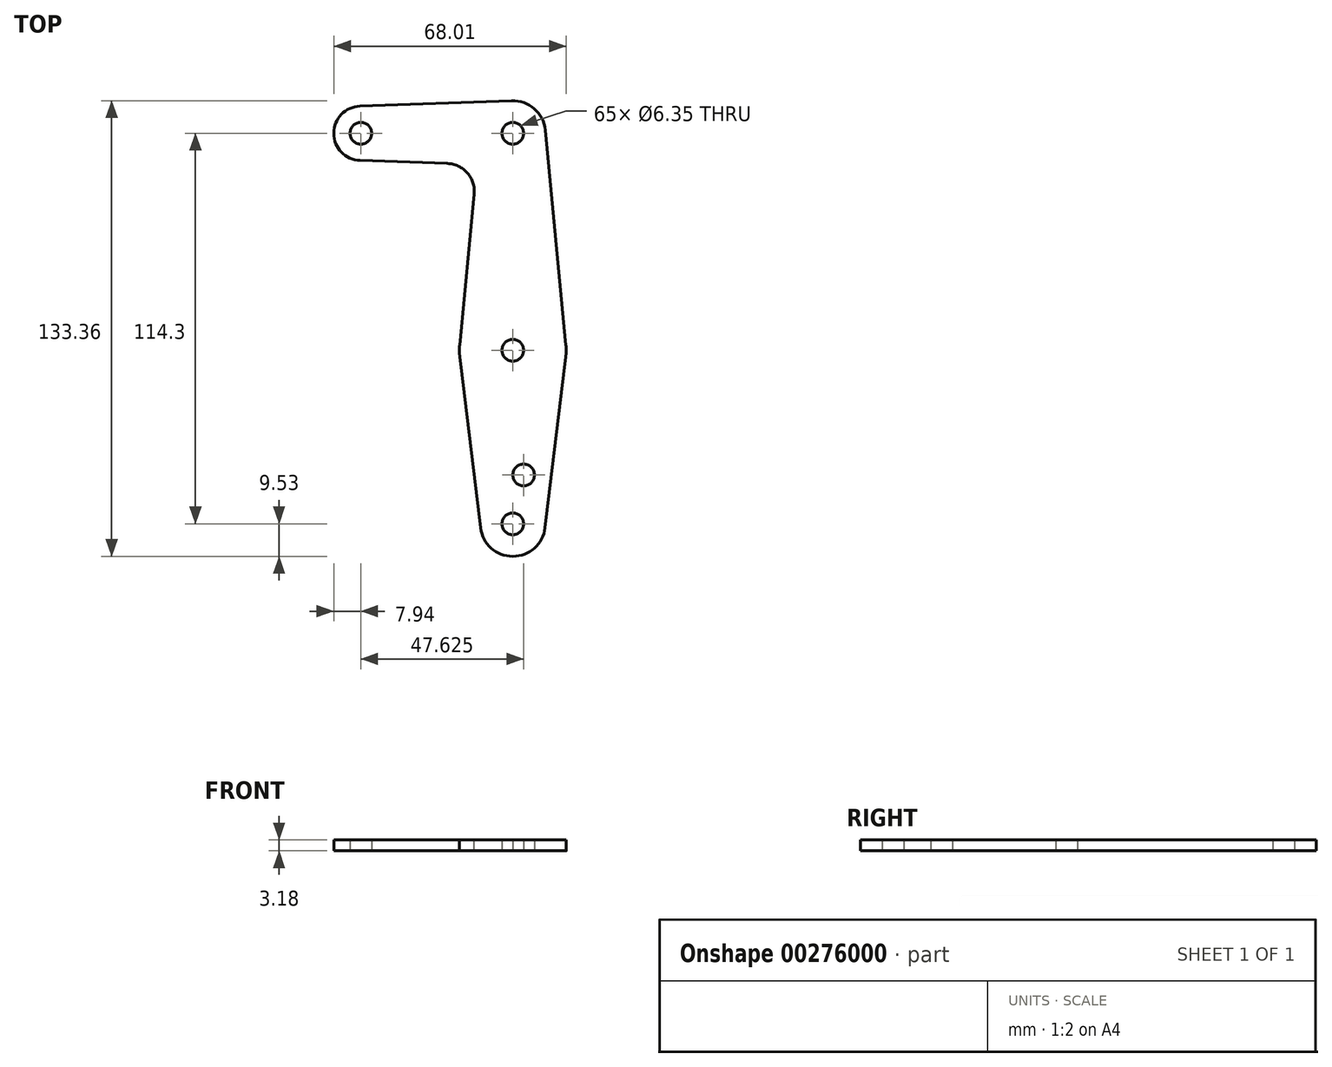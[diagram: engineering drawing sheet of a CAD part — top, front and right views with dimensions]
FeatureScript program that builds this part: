
annotation { "Feature Type Name" : "Feature", "Feature Type Description" : "" }
export const myFeature = defineFeature(function(context is Context, id is Id, definition is map)
    precondition{}
    {
        {
            var Q0;
            Q0=qCreatedBy(makeId("Top.planeOp"),FACE);
            var sketch = newSketch(context, id + "F0", { "sketchPlane" : qUnion([Q0])});
            skCircle(sketch, "E0", {"center": v(0, 0) * mm, "radius": 3.18 * mm});
            skLineSegment(sketch, "E1", {"start": v(0, 0) * mm, "end": v(-44.45, 0) * mm, "construction": true});
            skCircle(sketch, "E2", {"center": v(-44.45, 0) * mm, "radius": 3.18 * mm});
            skCircle(sketch, "E3", {"center": v(-44.45, 0) * mm, "radius": 7.94 * mm});
            skCircle(sketch, "E4", {"center": v(0, 0) * mm, "radius": 9.53 * mm});
            skLineSegment(sketch, "E5", {"start": v(0, 0) * mm, "end": v(0, -63.5) * mm, "construction": true});
            skCircle(sketch, "E6", {"center": v(0, -63.5) * mm, "radius": 3.18 * mm});
            skLineSegment(sketch, "E7", {"start": v(0, -63.5) * mm, "end": v(0, -114.3) * mm, "construction": true});
            skCircle(sketch, "E8", {"center": v(0, -114.3) * mm, "radius": 3.18 * mm});
            skLineSegment(sketch, "E9", {"start": v(0, -63.5) * mm, "end": v(3.18, -63.5) * mm, "construction": true});
            skLineSegment(sketch, "E10", {"start": v(3.18, -63.5) * mm, "end": v(3.18, -100.01) * mm, "construction": true});
            skCircle(sketch, "E11", {"center": v(3.18, -100.01) * mm, "radius": 3.18 * mm});
            skCircle(sketch, "E12", {"center": v(0, -114.3) * mm, "radius": 9.53 * mm});
            skCircle(sketch, "E13", {"center": v(0, -63.5) * mm, "radius": 15.62 * mm});
            skLineSegment(sketch, "E14", {"start": v(9.48, 0.91) * mm, "end": v(15.55, -62) * mm});
            skLineSegment(sketch, "E15", {"start": v(9.46, -115.44) * mm, "end": v(15.5, -65.37) * mm});
            skLineSegment(sketch, "E16", {"start": v(-44.73, -7.93) * mm, "end": v(0, -9.53) * mm});
            skLineSegment(sketch, "E17", {"start": v(-44.73, 7.93) * mm, "end": v(-0.34, 9.52) * mm});
            skLineSegment(sketch, "E18", {"start": v(-9.48, 0.91) * mm, "end": v(-15.55, -62) * mm});
            skLineSegment(sketch, "E19", {"start": v(-15.5, -65.37) * mm, "end": v(-9.46, -115.44) * mm});
            skSolve(sketch);
        }
        {
            var Q0;
            Q0=qSketchRegion(id+"F0",true);
            extrude(context, id + "F1", {"entities" : qUnion([Q0]), "depth" : 3.17 * mm});
        }
        {
            var Q0;
            Q0=makeQuery(id+"F1.opExtrude","SWEPT_EDGE",EDGE,{"disambiguationData":[OSD([sQuery(id+"F0.wireOp",EDGE,"E16"),sQuery(id+"F0.wireOp",EDGE,"E18")])]});
            fillet(context, id + "F2", {"entities" : qUnion([Q0]), "radius" : 8.2 * mm, "tangentPropagation" : true, "allowEdgeOverflow" : false});
        }
    });
